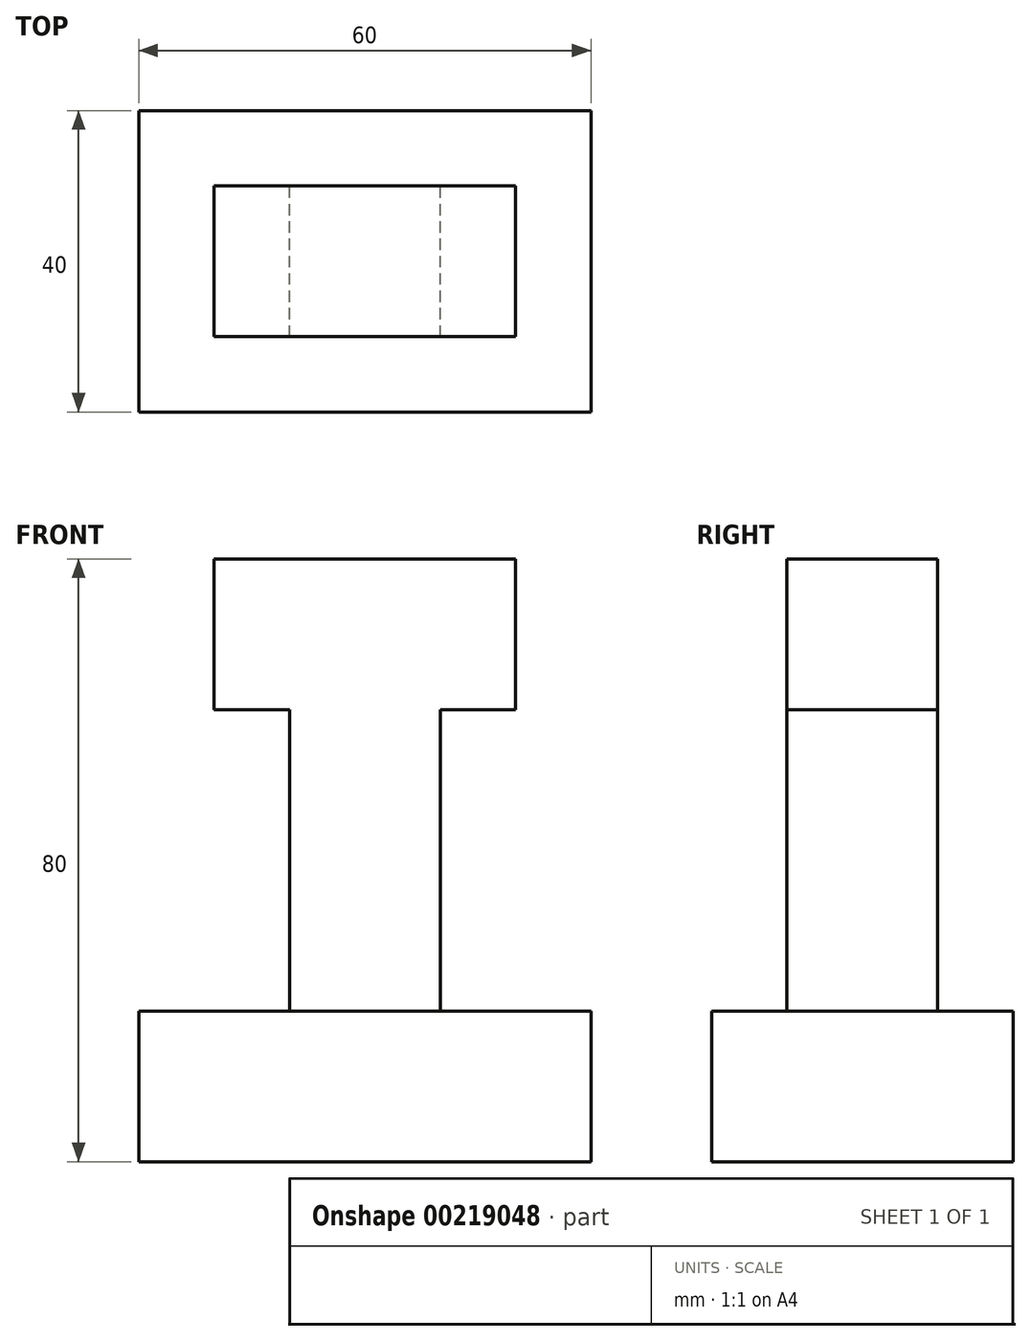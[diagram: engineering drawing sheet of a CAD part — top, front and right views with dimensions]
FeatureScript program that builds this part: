
annotation { "Feature Type Name" : "Feature", "Feature Type Description" : "" }
export const myFeature = defineFeature(function(context is Context, id is Id, definition is map)
    precondition{}
    {
        {
            var Q0;
            Q0=qCreatedBy(makeId("Front.planeOp"),FACE);
            var sketch = newSketch(context, id + "F0", { "sketchPlane" : qUnion([Q0])});
            skLineSegment(sketch, "E0", {"start": v(0, 0) * mm, "end": v(60, 0) * mm});
            skLineSegment(sketch, "E1", {"start": v(60, 0) * mm, "end": v(60, 20) * mm});
            skLineSegment(sketch, "E2", {"start": v(60, 20) * mm, "end": v(0, 20) * mm});
            skLineSegment(sketch, "E3", {"start": v(0, 20) * mm, "end": v(0, 0) * mm});
            skLineSegment(sketch, "E4", {"start": v(20, 20) * mm, "end": v(20, 60) * mm});
            skLineSegment(sketch, "E5", {"start": v(20, 60) * mm, "end": v(10, 60) * mm});
            skLineSegment(sketch, "E6", {"start": v(10, 60) * mm, "end": v(10, 80) * mm});
            skLineSegment(sketch, "E7", {"start": v(10, 80) * mm, "end": v(50, 80) * mm});
            skLineSegment(sketch, "E8", {"start": v(50, 80) * mm, "end": v(50, 60) * mm});
            skLineSegment(sketch, "E9", {"start": v(50, 60) * mm, "end": v(40, 60) * mm});
            skLineSegment(sketch, "E10", {"start": v(40, 60) * mm, "end": v(40, 20) * mm});
            skSolve(sketch);
        }
        {
            var Q0;
            Q0=makeQuery(id+"F0.imprint","IMPRINT",FACE,{"disambiguationData":[TD([[makeQuery(id+"F0.imprint","IMPRINT",EDGE,{"derivedFrom":sQuery(id+"F0.wireOp",EDGE,"E0")}),1.0]])]});
            extrude(context, id + "F1", {"entities" : qUnion([Q0]), "endBound" : BoundingType.SYMMETRIC, "depth" : 40 * mm});
        }
        {
            var Q0;
            {var subQ0=sQuery(id+"F0.wireOp",EDGE,"E4");Q0=makeQuery(id+"F0.imprint","IMPRINT",FACE,{"disambiguationData":[TD([[makeQuery(id+"F0.imprint","IMPRINT",EDGE,{"derivedFrom":subQ0}),-1.0]])]});}
            extrude(context, id + "F2", {"entities" : qUnion([Q0]), "operationType" : NewBodyOperationType.ADD, "endBound" : BoundingType.SYMMETRIC, "depth" : 20 * mm});
        }
    });
